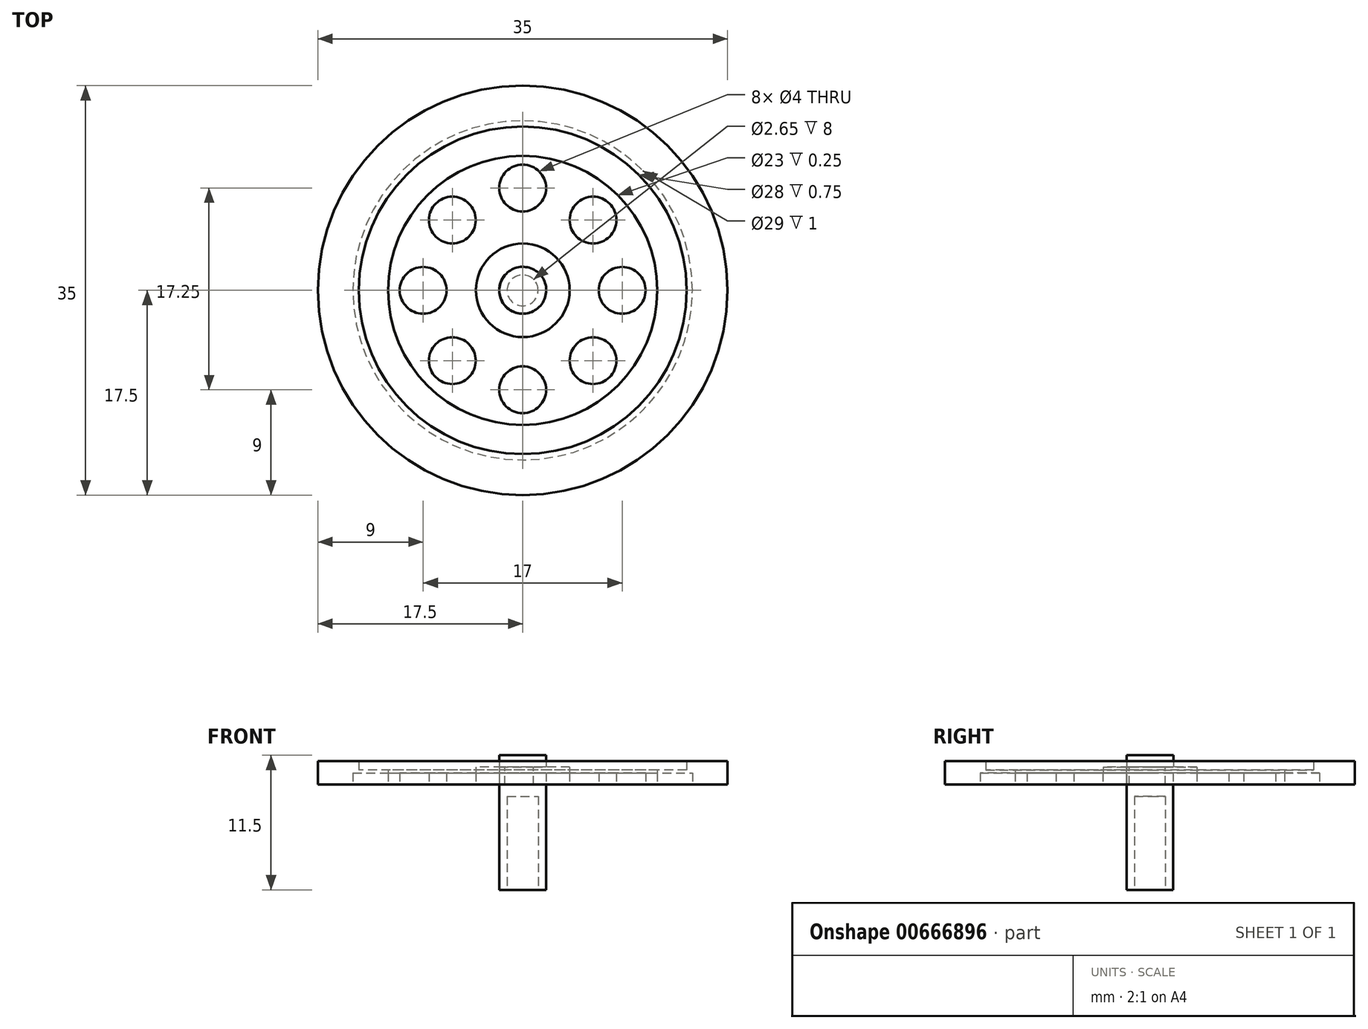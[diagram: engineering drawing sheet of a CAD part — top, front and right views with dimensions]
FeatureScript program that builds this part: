
annotation { "Feature Type Name" : "Feature", "Feature Type Description" : "" }
export const myFeature = defineFeature(function(context is Context, id is Id, definition is map)
    precondition{}
    {
        {
            var Q0;
            Q0=qCreatedBy(makeId("Top.planeOp"),FACE);
            var sketch = newSketch(context, id + "F0", { "sketchPlane" : qUnion([Q0])});
            skCircle(sketch, "E0", {"center": v(17.5, 17.5) * mm, "radius": 17.5 * mm});
            skSolve(sketch);
        }
        {
            var Q0;
            Q0=makeQuery(id+"F0.imprint","IMPRINT",FACE,{"disambiguationData":[TD([[makeQuery(id+"F0.imprint","IMPRINT",EDGE,{"derivedFrom":sQuery(id+"F0.wireOp",EDGE,"E0")}),1.0]])]});
            var sketch = newSketch(context, id + "F1", { "sketchPlane" : qUnion([Q0])});
            skCircle(sketch, "E1", {"center": v(17.5, 17.5) * mm, "radius": 14 * mm});
            skCircle(sketch, "E2", {"center": v(17.5, 17.5) * mm, "radius": 11.5 * mm});
            skCircle(sketch, "E3", {"center": v(17.5, 17.5) * mm, "radius": 5.5 * mm});
            skCircle(sketch, "E4", {"center": v(17.5, 17.5) * mm, "radius": 2 * mm});
            skCircle(sketch, "E5", {"center": v(17.5, 26.25) * mm, "radius": 2 * mm});
            skCircle(sketch, "E6", {"center": v(23.51, 23.51) * mm, "radius": 2 * mm});
            skCircle(sketch, "E7", {"center": v(26, 17.5) * mm, "radius": 2 * mm});
            skCircle(sketch, "E8", {"center": v(23.51, 11.49) * mm, "radius": 2 * mm});
            skCircle(sketch, "E9", {"center": v(17.5, 9) * mm, "radius": 2 * mm});
            skCircle(sketch, "E10", {"center": v(11.49, 11.49) * mm, "radius": 2 * mm});
            skCircle(sketch, "E11", {"center": v(9, 17.5) * mm, "radius": 2 * mm});
            skCircle(sketch, "E12", {"center": v(11.49, 23.51) * mm, "radius": 2 * mm});
            skSolve(sketch);
        }
        {
            var Q0;
            Q0=makeQuery(id+"F1.imprint","IMPRINT",FACE,{"disambiguationData":[TD([[makeQuery(id+"F1.imprint","IMPRINT",EDGE,{"derivedFrom":sQuery(id+"F1.wireOp",EDGE,"E3")}),1.0]])]});
            extrude(context, id + "F2", {"entities" : qUnion([Q0]), "depth" : 1 * mm, "offsetDistance" : 25 * mm});
        }
        {
            var Q0;
            Q0=makeQuery(id+"F1.imprint","IMPRINT",FACE,{"disambiguationData":[TD([[makeQuery(id+"F1.imprint","IMPRINT",EDGE,{"derivedFrom":sQuery(id+"F1.wireOp",EDGE,"E2")}),1.0]])]});
            extrude(context, id + "F3", {"entities" : qUnion([Q0]), "operationType" : NewBodyOperationType.ADD, "depth" : 1 * mm, "offsetDistance" : 25 * mm});
        }
        {
            var Q0;
            Q0=makeQuery(id+"F1.imprint","IMPRINT",FACE,{"disambiguationData":[TD([[makeQuery(id+"F1.imprint","IMPRINT",EDGE,{"derivedFrom":sQuery(id+"F1.wireOp",EDGE,"E1")}),1.0]])]});
            extrude(context, id + "F4", {"entities" : qUnion([Q0]), "operationType" : NewBodyOperationType.ADD, "depth" : 1.25 * mm, "offsetDistance" : 25 * mm});
        }
        {
            var Q0;
            Q0=makeQuery(id+"F1.imprint","IMPRINT",FACE,{"disambiguationData":[TD([[makeQuery(id+"F1.imprint","IMPRINT",EDGE,{"derivedFrom":sQuery(id+"F1.wireOp",EDGE,"E1")}),-1.0]])]});
            extrude(context, id + "F5", {"entities" : qUnion([Q0]), "operationType" : NewBodyOperationType.ADD, "depth" : 2 * mm, "offsetDistance" : 25 * mm});
        }
        {
            var Q0;
            Q0=makeQuery(id+"F3.opExtrude","CAP_FACE",FACE,{"disambiguationData":[OSD([sQuery(id+"F1.wireOp",EDGE,"E2"),sQuery(id+"F1.wireOp",EDGE,"E3"),sQuery(id+"F1.wireOp",EDGE,"E5"),sQuery(id+"F1.wireOp",EDGE,"E6"),sQuery(id+"F1.wireOp",EDGE,"E7"),sQuery(id+"F1.wireOp",EDGE,"E8"),sQuery(id+"F1.wireOp",EDGE,"E9"),sQuery(id+"F1.wireOp",EDGE,"E10"),sQuery(id+"F1.wireOp",EDGE,"E11"),sQuery(id+"F1.wireOp",EDGE,"E12")])],"isStart":false});
            var sketch = newSketch(context, id + "F6", { "sketchPlane" : qUnion([Q0])});
            skCircle(sketch, "E13", {"center": v(17.51, 17.5) * mm, "radius": 2 * mm});
            skPoint(sketch, "E13.first.point", {"position": v(17.4, 19.5) * mm});
            skPoint(sketch, "E13.second.point", {"position": v(17.6, 15.5) * mm});
            skPoint(sketch, "E13.third.point", {"position": v(19.42, 16.9) * mm});
            skSolve(sketch);
        }
        {
            var Q0;
            Q0=makeQuery(id+"F6.imprint","IMPRINT",FACE,{"disambiguationData":[TD([[makeQuery(id+"F6.imprint","IMPRINT",EDGE,{"derivedFrom":sQuery(id+"F6.wireOp",EDGE,"E13")}),1.0]])]});
            extrude(context, id + "F7", {"entities" : qUnion([Q0]), "operationType" : NewBodyOperationType.ADD, "depth" : 1.5 * mm, "offsetDistance" : 25 * mm});
        }
        {
            var Q0;
            {var subQ0=sQuery(id+"F1.wireOp",EDGE,"E1");var subQ1=sQuery(id+"F1.wireOp",EDGE,"E2");var subQ2=sQuery(id+"F1.wireOp",EDGE,"E3");Q0=makeQuery(id+"F5.boolean.opBoolean","MERGE",FACE,{"derivedFrom":[makeQuery(id+"F4.boolean.opBoolean","MERGE",FACE,{"derivedFrom":[makeQuery(id+"F3.boolean.opBoolean","MERGE",FACE,{"derivedFrom":[makeQuery(id+"F2.opExtrude","CAP_FACE",FACE,{"disambiguationData":[OSD([subQ2,sQuery(id+"F1.wireOp",EDGE,"E4")])],"isStart":true}),makeQuery(id+"F3.opExtrude","CAP_FACE",FACE,{"disambiguationData":[OSD([subQ1,subQ2,sQuery(id+"F1.wireOp",EDGE,"E5"),sQuery(id+"F1.wireOp",EDGE,"E6"),sQuery(id+"F1.wireOp",EDGE,"E7"),sQuery(id+"F1.wireOp",EDGE,"E8"),sQuery(id+"F1.wireOp",EDGE,"E9"),sQuery(id+"F1.wireOp",EDGE,"E10"),sQuery(id+"F1.wireOp",EDGE,"E11"),sQuery(id+"F1.wireOp",EDGE,"E12")])],"isStart":true})]}),makeQuery(id+"F4.opExtrude","CAP_FACE",FACE,{"disambiguationData":[OSD([subQ0,subQ1])],"isStart":true})]}),makeQuery(id+"F5.opExtrude","CAP_FACE",FACE,{"disambiguationData":[OSD([sQuery(id+"F0.wireOp",EDGE,"E0"),subQ0])],"isStart":true})]});}
            var sketch = newSketch(context, id + "F8", { "sketchPlane" : qUnion([Q0])});
            skCircle(sketch, "E14", {"center": v(17.5, -17.5) * mm, "radius": 17.5 * mm});
            skPoint(sketch, "E14.first.point", {"position": v(15.72, -0.1) * mm});
            skPoint(sketch, "E14.second.point", {"position": v(34.13, -22.94) * mm});
            skPoint(sketch, "E14.third.point", {"position": v(10.99, -33.74) * mm});
            skCircle(sketch, "E15", {"center": v(17.5, -17.5) * mm, "radius": 11.5 * mm});
            skCircle(sketch, "E16", {"center": v(17.5, -17.5) * mm, "radius": 14.5 * mm});
            skSolve(sketch);
        }
        {
            var Q0;
            Q0=makeQuery(id+"F8.imprint","IMPRINT",FACE,{"disambiguationData":[TD([[makeQuery(id+"F8.imprint","IMPRINT",EDGE,{"derivedFrom":sQuery(id+"F8.wireOp",EDGE,"E15")}),-1.0]])]});
            extrude(context, id + "F9", {"entities" : qUnion([Q0]), "operationType" : NewBodyOperationType.REMOVE, "oppositeDirection" : true, "depth" : 1 * mm, "offsetDistance" : 25 * mm});
        }
        {
            var Q0;
            Q0=makeQuery(id+"F7.opExtrude","CAP_FACE",FACE,{"disambiguationData":[OSD([sQuery(id+"F6.wireOp",EDGE,"E13")])],"isStart":true});
            extrude(context, id + "F10", {"entities" : qUnion([Q0]), "operationType" : NewBodyOperationType.ADD, "depth" : 10 * mm, "offsetDistance" : 25 * mm});
        }
        {
            var Q0;
            Q0=makeQuery(id+"F10.opExtrude","CAP_FACE",FACE,{"disambiguationData":[OSD([sQuery(id+"F6.wireOp",EDGE,"E13")])],"isStart":false});
            var sketch = newSketch(context, id + "F11", { "sketchPlane" : qUnion([Q0])});
            skCircle(sketch, "E17", {"center": v(17.5, -17.5) * mm, "radius": 2 * mm});
            skPoint(sketch, "E17.first.point", {"position": v(18.43, -15.73) * mm});
            skPoint(sketch, "E17.second.point", {"position": v(17.82, -19.47) * mm});
            skPoint(sketch, "E17.third.point", {"position": v(15.99, -18.8) * mm});
            skCircle(sketch, "E18", {"center": v(17.5, -17.5) * mm, "radius": 1.33 * mm});
            skSolve(sketch);
        }
        {
            var Q0;
            Q0=makeQuery(id+"F11.imprint","IMPRINT",FACE,{"disambiguationData":[TD([[makeQuery(id+"F11.imprint","IMPRINT",EDGE,{"derivedFrom":sQuery(id+"F11.wireOp",EDGE,"E18")}),1.0]])]});
            var Q1;
            Q1=sQuery(id+"F11.wireOp",EDGE,"E18");
            extrude(context, id + "F12", {"entities" : qUnion([Q0]), "operationType" : NewBodyOperationType.REMOVE, "surfaceEntities" : qUnion([Q1]), "oppositeDirection" : true, "depth" : 8 * mm, "offsetDistance" : 25 * mm});
        }
        {
            var Q0;
            {var subQ0=sQuery(id+"F1.wireOp",EDGE,"E3");Q0=makeQuery(id+"F3.boolean.opBoolean","MERGE",FACE,{"derivedFrom":[makeQuery(id+"F2.opExtrude","CAP_FACE",FACE,{"disambiguationData":[OSD([subQ0,sQuery(id+"F1.wireOp",EDGE,"E4")])],"isStart":false}),makeQuery(id+"F3.opExtrude","CAP_FACE",FACE,{"disambiguationData":[OSD([sQuery(id+"F1.wireOp",EDGE,"E2"),subQ0,sQuery(id+"F1.wireOp",EDGE,"E5"),sQuery(id+"F1.wireOp",EDGE,"E6"),sQuery(id+"F1.wireOp",EDGE,"E7"),sQuery(id+"F1.wireOp",EDGE,"E8"),sQuery(id+"F1.wireOp",EDGE,"E9"),sQuery(id+"F1.wireOp",EDGE,"E10"),sQuery(id+"F1.wireOp",EDGE,"E11"),sQuery(id+"F1.wireOp",EDGE,"E12")])],"isStart":false})]});}
            var sketch = newSketch(context, id + "F13", { "sketchPlane" : qUnion([Q0])});
            skCircle(sketch, "E19", {"center": v(17.51, 17.5) * mm, "radius": 4 * mm});
            skSolve(sketch);
        }
        {
            var Q0;
            Q0=makeQuery(id+"F13.imprint","IMPRINT",FACE,{"disambiguationData":[TD([[makeQuery(id+"F13.imprint","IMPRINT",EDGE,{"derivedFrom":sQuery(id+"F13.wireOp",EDGE,"E19")}),1.0]])]});
            extrude(context, id + "F14", {"entities" : qUnion([Q0]), "operationType" : NewBodyOperationType.ADD, "depth" : .5 * mm, "offsetDistance" : 25 * mm});
        }
    });
